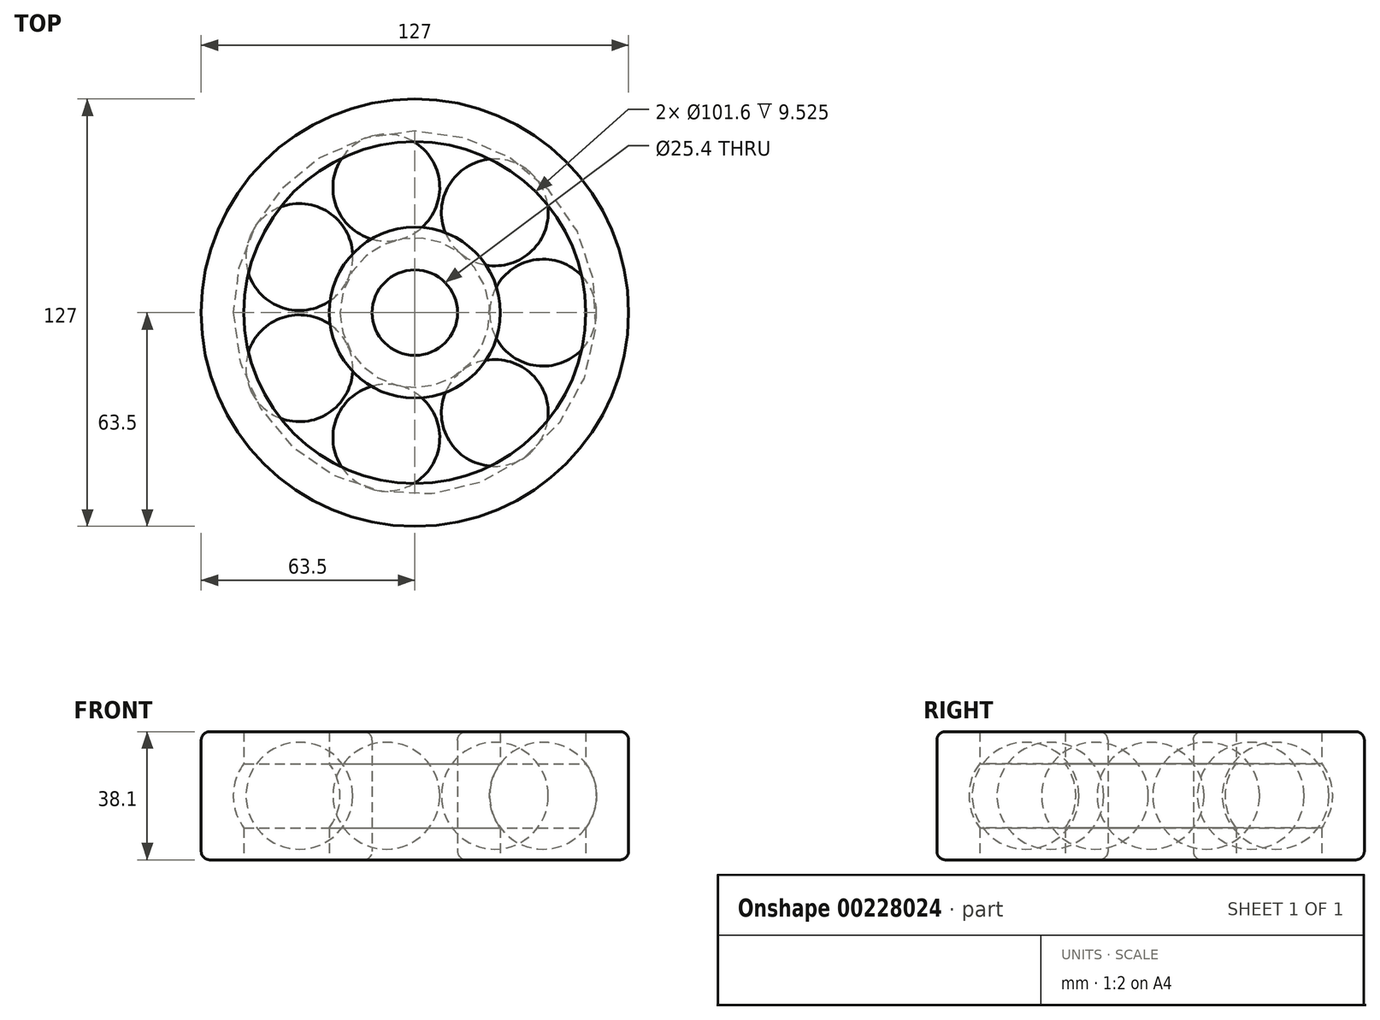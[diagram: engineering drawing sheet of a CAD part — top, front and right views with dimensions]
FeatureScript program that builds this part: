
annotation { "Feature Type Name" : "Feature", "Feature Type Description" : "" }
export const myFeature = defineFeature(function(context is Context, id is Id, definition is map)
    precondition{}
    {
        {
            var Q0;
            Q0=qCreatedBy(makeId("Front.planeOp"),FACE);
            var sketch = newSketch(context, id + "F0", { "sketchPlane" : qUnion([Q0])});
            skLineSegment(sketch, "E0", {"start": v(0, 0) * mm, "end": v(63.5, 0) * mm, "construction": true});
            skLineSegment(sketch, "E1.bottom", {"start": v(50.8, -19.05) * mm, "end": v(63.5, -19.05) * mm});
            skLineSegment(sketch, "E1.top", {"start": v(50.8, 19.05) * mm, "end": v(63.5, 19.05) * mm});
            skLineSegment(sketch, "E1.left", {"start": v(50.8, -19.05) * mm, "end": v(50.8, 19.05) * mm});
            skLineSegment(sketch, "E1.right", {"start": v(63.5, -19.05) * mm, "end": v(63.5, 19.05) * mm});
            skPoint(sketch, "E1.middle", {"position": v(57.15, 0) * mm});
            skLineSegment(sketch, "E2.bottom", {"start": v(12.7, -19.05) * mm, "end": v(25.4, -19.05) * mm});
            skLineSegment(sketch, "E2.top", {"start": v(12.7, 19.05) * mm, "end": v(25.4, 19.05) * mm});
            skLineSegment(sketch, "E2.left", {"start": v(12.7, -19.05) * mm, "end": v(12.7, 19.05) * mm});
            skLineSegment(sketch, "E2.right", {"start": v(25.4, -19.05) * mm, "end": v(25.4, 19.05) * mm});
            skPoint(sketch, "E2.middle", {"position": v(19.05, 0) * mm});
            skCircle(sketch, "E3", {"center": v(38.1, 0) * mm, "radius": 15.88 * mm});
            skLineSegment(sketch, "E4", {"start": v(57.15, 0) * mm, "end": v(19.05, 0) * mm});
            skLineSegment(sketch, "E5", {"start": v(0, 0) * mm, "end": v(0, 17.93) * mm, "construction": true});
            skSolve(sketch);
        }
        {
            var Q0;
            {var subQ4=sQuery(id+"F0.wireOp",EDGE,"E1.bottom");Q0=makeQuery(id+"F0.imprint","IMPRINT",FACE,{"disambiguationData":[TD([[makeQuery(id+"F0.imprint","IMPRINT",EDGE,{"derivedFrom":subQ4}),1.0]])]});}
            var Q1;
            {var subQ1=sQuery(id+"F0.wireOp",EDGE,"E2.bottom");Q1=makeQuery(id+"F0.imprint","IMPRINT",FACE,{"disambiguationData":[TD([[makeQuery(id+"F0.imprint","IMPRINT",EDGE,{"derivedFrom":subQ1}),1.0]])]});}
            var Q2;
            Q2=sQuery(id+"F0.wireOp",EDGE,"E5");
            revolve(context, id + "F1", {"entities" : qUnion([Q0, Q1]), "axis" : qUnion([Q2]), "revolveType" : RevolveType.FULL});
        }
        {
            var Q0;
            {var subQ0=sQuery(id+"F0.wireOp",EDGE,"E3");var subQ1=sQuery(id+"F0.wireOp",EDGE,"E1.left");var subQ2=makeQuery(id+"F0.imprint","INTERSECT",VERTEX,{"disambiguationData":[OD(1.0)],"derivedFrom":[subQ1,subQ0]});Q0=makeQuery(id+"F0.imprint","IMPRINT",FACE,{"disambiguationData":[TD([[makeQuery(id+"F0.imprint","IMPRINT",EDGE,{"disambiguationData":[TD([[subQ2,1.0]])],"derivedFrom":subQ1}),1.0]])]});}
            var Q1;
            {var subQ0=sQuery(id+"F0.wireOp",EDGE,"E3");var subQ1=sQuery(id+"F0.wireOp",EDGE,"E2.right");var subQ2=makeQuery(id+"F0.imprint","INTERSECT",VERTEX,{"disambiguationData":[OD(1.0)],"derivedFrom":[subQ1,subQ0]});Q1=makeQuery(id+"F0.imprint","IMPRINT",FACE,{"disambiguationData":[TD([[makeQuery(id+"F0.imprint","IMPRINT",EDGE,{"disambiguationData":[TD([[subQ2,1.0]])],"derivedFrom":subQ1}),1.0]])]});}
            var Q2;
            {var subQ0=sQuery(id+"F0.wireOp",EDGE,"E3");var subQ1=sQuery(id+"F0.wireOp",EDGE,"E1.left");var subQ2=makeQuery(id+"F0.imprint","INTERSECT",VERTEX,{"disambiguationData":[OD(1.0)],"derivedFrom":[subQ1,subQ0]});Q2=makeQuery(id+"F0.imprint","IMPRINT",FACE,{"disambiguationData":[TD([[makeQuery(id+"F0.imprint","IMPRINT",EDGE,{"disambiguationData":[TD([[subQ2,1.0]])],"derivedFrom":subQ1}),-1.0]])]});}
            var Q3;
            Q3=sQuery(id+"F0.wireOp",EDGE,"E4");
            revolve(context, id + "F2", {"entities" : qUnion([Q0, Q1, Q2]), "axis" : qUnion([Q3]), "revolveType" : RevolveType.FULL});
        }
        {
            var Q0;
            Q0=makeQuery(id+"F2.opRevolve","SWEPT_BODY",BODY,{"disambiguationData":[OSD([sQuery(id+"F0.wireOp",EDGE,"E3"),sQuery(id+"F0.wireOp",EDGE,"E4")])]});
            var Q1;
            Q1=sQuery(id+"F0.wireOp",EDGE,"E5");
            circularPattern(context, id + "F3", {"entities" : qUnion([Q0]), "axis" : qUnion([Q1]), "angle" : 360 * degree, "instanceCount" : 7, "equalSpace" : true});
        }
        {
            var Q0;
            Q0=makeQuery(id+"F1.opRevolve","SWEPT_EDGE",EDGE,{"disambiguationData":[OSD([sQuery(id+"F0.wireOp",EDGE,"E1.bottom"),sQuery(id+"F0.wireOp",EDGE,"E1.right")])]});
            var Q1;
            Q1=makeQuery(id+"F1.opRevolve","SWEPT_EDGE",EDGE,{"disambiguationData":[OSD([sQuery(id+"F0.wireOp",EDGE,"E1.top"),sQuery(id+"F0.wireOp",EDGE,"E1.right")])]});
            var Q2;
            Q2=makeQuery(id+"F1.opRevolve","SWEPT_EDGE",EDGE,{"disambiguationData":[OSD([sQuery(id+"F0.wireOp",EDGE,"E2.top"),sQuery(id+"F0.wireOp",EDGE,"E2.left")])]});
            var Q3;
            Q3=makeQuery(id+"F1.opRevolve","SWEPT_EDGE",EDGE,{"disambiguationData":[OSD([sQuery(id+"F0.wireOp",EDGE,"E2.bottom"),sQuery(id+"F0.wireOp",EDGE,"E2.left")])]});
            fillet(context, id + "F4", {"entities" : qUnion([Q0, Q1, Q2, Q3]), "radius" : 2.54 * mm, "tangentPropagation" : true, "allowEdgeOverflow" : false});
        }
    });
